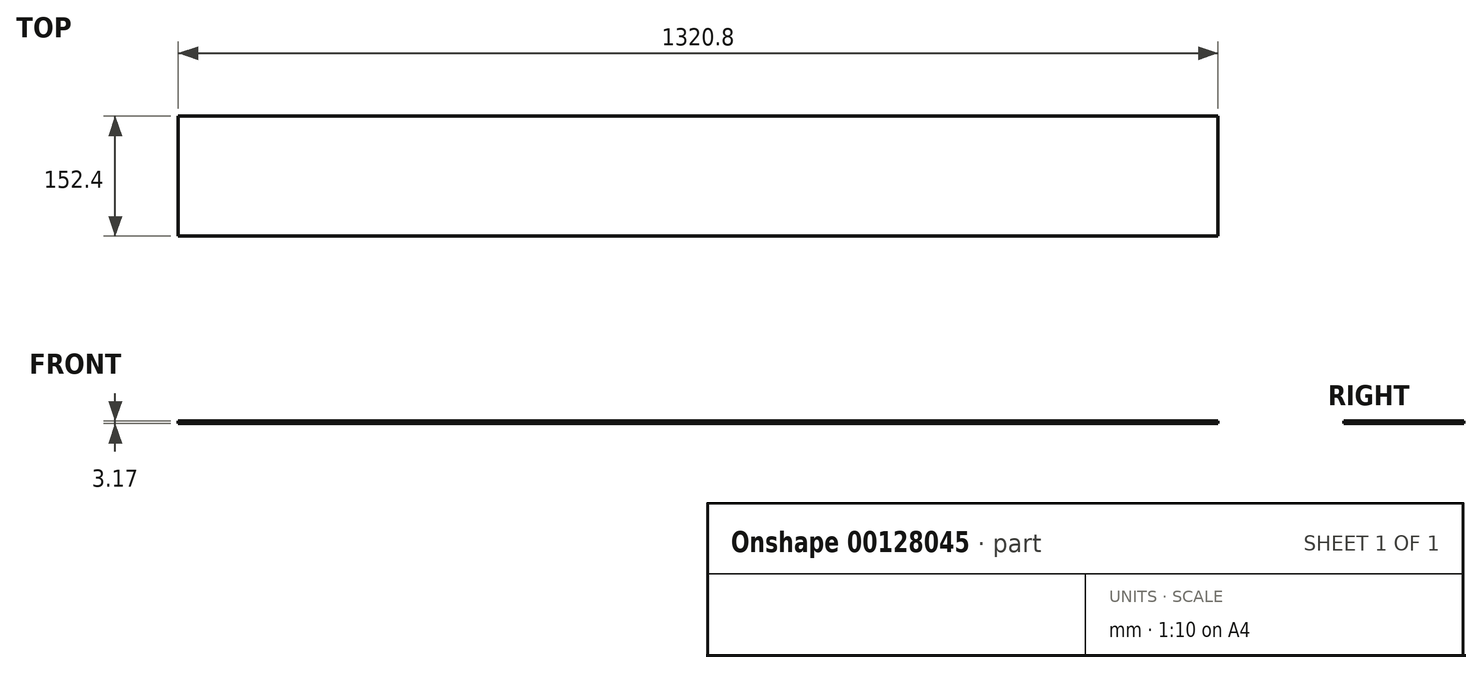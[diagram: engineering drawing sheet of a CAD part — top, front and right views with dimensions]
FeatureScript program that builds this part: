
annotation { "Feature Type Name" : "Feature", "Feature Type Description" : "" }
export const myFeature = defineFeature(function(context is Context, id is Id, definition is map)
    precondition{}
    {
        {
            var Q0;
            Q0=qCreatedBy(makeId("Top.planeOp"),FACE);
            var sketch = newSketch(context, id + "F0", { "sketchPlane" : qUnion([Q0])});
            skLineSegment(sketch, "E0.bottom", {"start": v(660.4, 76.2) * mm, "end": v(-660.4, 76.2) * mm});
            skLineSegment(sketch, "E0.top", {"start": v(660.4, -76.2) * mm, "end": v(-660.4, -76.2) * mm});
            skLineSegment(sketch, "E0.left", {"start": v(660.4, 76.2) * mm, "end": v(660.4, -76.2) * mm});
            skLineSegment(sketch, "E0.right", {"start": v(-660.4, 76.2) * mm, "end": v(-660.4, -76.2) * mm});
            skPoint(sketch, "E0.middle", {"position": v(0, 0) * mm});
            skSolve(sketch);
        }
        {
            var Q0;
            Q0=makeQuery(id+"F0.imprint","IMPRINT",FACE,{"disambiguationData":[TD([[makeQuery(id+"F0.imprint","IMPRINT",EDGE,{"derivedFrom":sQuery(id+"F0.wireOp",EDGE,"E0.bottom")}),1.0]])]});
            extrude(context, id + "F1", {"entities" : qUnion([Q0]), "oppositeDirection" : true, "depth" : 3.17 * mm});
        }
    });
